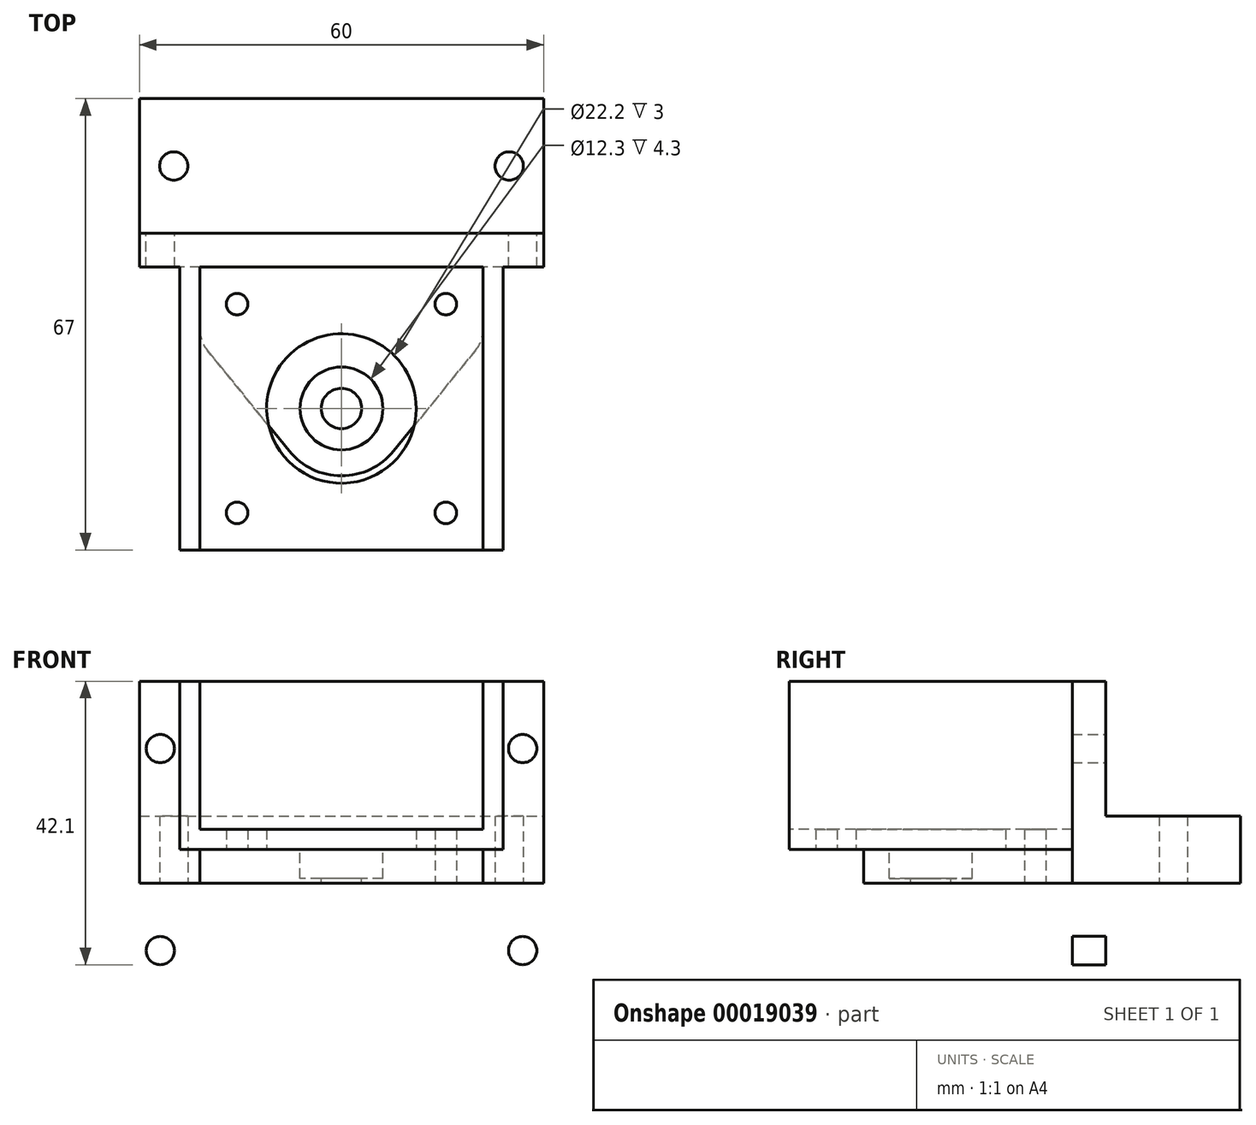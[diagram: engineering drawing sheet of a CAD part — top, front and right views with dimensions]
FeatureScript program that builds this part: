
annotation { "Feature Type Name" : "Feature", "Feature Type Description" : "" }
export const myFeature = defineFeature(function(context is Context, id is Id, definition is map)
    precondition{}
    {
        {
            var Q0;
            Q0=qCreatedBy(makeId("Top.planeOp"),FACE);
            var sketch = newSketch(context, id + "F0", { "sketchPlane" : qUnion([Q0])});
            skLineSegment(sketch, "E0.bottom", {"start": v(-30, 0) * mm, "end": v(30, 0) * mm});
            skLineSegment(sketch, "E0.top", {"start": v(-30, -20) * mm, "end": v(30, -20) * mm});
            skLineSegment(sketch, "E0.left", {"start": v(-30, 0) * mm, "end": v(-30, -20) * mm});
            skLineSegment(sketch, "E0.right", {"start": v(30, 0) * mm, "end": v(30, -20) * mm});
            skCircle(sketch, "E1", {"center": v(-24.9, -10) * mm, "radius": 2.1 * mm});
            skPoint(sketch, "E1.centerSnap0", {"position": v(-30, -10) * mm});
            skCircle(sketch, "E2.MirrorC", {"center": v(24.9, -10) * mm, "radius": 2.1 * mm});
            skLineSegment(sketch, "E3", {"start": v(-30, -20) * mm, "end": v(-30, -25) * mm});
            skLineSegment(sketch, "E4", {"start": v(-30, -25) * mm, "end": v(30, -25) * mm});
            skLineSegment(sketch, "E5", {"start": v(30, -25) * mm, "end": v(30, -20) * mm});
            skLineSegment(sketch, "E6.bottom", {"start": v(-21, -67) * mm, "end": v(21, -67) * mm});
            skCircle(sketch, "E7", {"center": v(-15.5, -30.5) * mm, "radius": 1.6 * mm});
            skCircle(sketch, "E8.MirrorC", {"center": v(15.5, -30.5) * mm, "radius": 1.6 * mm});
            skCircle(sketch, "E9", {"center": v(-15.5, -61.5) * mm, "radius": 1.6 * mm});
            skCircle(sketch, "E10.MirrorC", {"center": v(15.5, -61.5) * mm, "radius": 1.6 * mm});
            skLineSegment(sketch, "E11", {"start": v(15.5, -28.9) * mm, "end": v(15.5, -25) * mm, "construction": true});
            skLineSegment(sketch, "E12", {"start": v(15.5, -63.1) * mm, "end": v(15.5, -67) * mm, "construction": true});
            skLineSegment(sketch, "E13", {"start": v(-17.1, -30.5) * mm, "end": v(-21, -30.5) * mm, "construction": true});
            skLineSegment(sketch, "E14", {"start": v(-21, -25) * mm, "end": v(-21, -67) * mm});
            skLineSegment(sketch, "E15.MirrorCS", {"start": v(21, -25) * mm, "end": v(21, -67) * mm});
            skLineSegment(sketch, "E16", {"start": v(17.1, -30.5) * mm, "end": v(21, -30.5) * mm, "construction": true});
            skLineSegment(sketch, "E17", {"start": v(17.1, -61.5) * mm, "end": v(21, -61.5) * mm, "construction": true});
            skLineSegment(sketch, "E18.0", {"start": v(-24, -25) * mm, "end": v(-24, -67) * mm});
            skLineSegment(sketch, "E19.MirrorCS", {"start": v(24, -25) * mm, "end": v(24, -67) * mm});
            skLineSegment(sketch, "E20.0", {"start": v(-21, -70) * mm, "end": v(21, -70) * mm});
            skLineSegment(sketch, "E21", {"start": v(-24, -67) * mm, "end": v(-21, -70) * mm});
            skLineSegment(sketch, "E22", {"start": v(24, -67) * mm, "end": v(21, -70) * mm});
            skLineSegment(sketch, "E23", {"start": v(0, -67) * mm, "end": v(0, -25) * mm, "construction": true});
            skLineSegment(sketch, "E24", {"start": v(-21, -46) * mm, "end": v(21, -46) * mm, "construction": true});
            skCircle(sketch, "E25", {"center": v(0, -46) * mm, "radius": 11.1 * mm});
            skSolve(sketch);
        }
        {
            var Q0;
            Q0=makeQuery(id+"F0.imprint","IMPRINT",FACE,{"disambiguationData":[TD([[makeQuery(id+"F0.imprint","IMPRINT",EDGE,{"derivedFrom":sQuery(id+"F0.wireOp",EDGE,"E0.bottom")}),-1.0]])]});
            extrude(context, id + "F1", {"entities" : qUnion([Q0]), "depth" : 5 * mm});
        }
        {
            var Q0;
            Q0=makeQuery(id+"F1.opExtrude","SWEPT_FACE",FACE,{"disambiguationData":[OSD([sQuery(id+"F0.wireOp",EDGE,"E0.top")])]});
            var sketch = newSketch(context, id + "F2", { "sketchPlane" : qUnion([Q0])});
            skLineSegment(sketch, "E26.bottom", {"start": v(-30, 25) * mm, "end": v(30, 25) * mm});
            skLineSegment(sketch, "E26.top", {"start": v(-30, 5) * mm, "end": v(30, 5) * mm});
            skLineSegment(sketch, "E26.left", {"start": v(-30, 25) * mm, "end": v(-30, 5) * mm});
            skLineSegment(sketch, "E26.right", {"start": v(30, 25) * mm, "end": v(30, 5) * mm});
            skCircle(sketch, "E27", {"center": v(-26.9, 15) * mm, "radius": 2.1 * mm});
            skPoint(sketch, "E27.centerSnap0", {"position": v(-30, 15) * mm});
            skCircle(sketch, "E28.MirrorC", {"center": v(26.9, 15) * mm, "radius": 2.1 * mm});
            skLineSegment(sketch, "E29.0", {"start": v(-30, 5) * mm, "end": v(-30, 0) * mm});
            skLineSegment(sketch, "E29.1", {"start": v(-30, 0) * mm, "end": v(30, 0) * mm});
            skLineSegment(sketch, "E29.2", {"start": v(30, 5) * mm, "end": v(30, 0) * mm});
            skSolve(sketch);
        }
        {
            var Q0;
            Q0=makeQuery(id+"F2.imprint","IMPRINT",FACE,{"disambiguationData":[TD([[makeQuery(id+"F2.imprint","IMPRINT",EDGE,{"derivedFrom":sQuery(id+"F2.wireOp",EDGE,"E26.top")}),-1.0]])]});
            var Q1;
            Q1=makeQuery(id+"F2.imprint","IMPRINT",FACE,{"disambiguationData":[TD([[makeQuery(id+"F2.imprint","IMPRINT",EDGE,{"derivedFrom":sQuery(id+"F2.wireOp",EDGE,"E26.bottom")}),-1.0]])]});
            extrude(context, id + "F3", {"entities" : qUnion([Q0, Q1]), "operationType" : NewBodyOperationType.ADD, "depth" : 5 * mm});
        }
        {
            var Q0;
            Q0=makeQuery(id+"F0.imprint","IMPRINT",FACE,{"disambiguationData":[TD([[makeQuery(id+"F0.imprint","IMPRINT",EDGE,{"derivedFrom":sQuery(id+"F0.wireOp",EDGE,"E6.bottom")}),-1.0]])]});
            var Q1;
            Q1=makeQuery(id+"F3.opExtrude","SWEPT_FACE",FACE,{"disambiguationData":[OSD([sQuery(id+"F2.wireOp",EDGE,"E26.bottom")])]});
            extrude(context, id + "F4", {"entities" : qUnion([Q0]), "operationType" : NewBodyOperationType.ADD, "endBound" : BoundingType.UP_TO_SURFACE, "endBoundEntityFace" : qUnion([Q1]), "depth" : 25 * mm});
        }
        {
            var Q0;
            Q0=makeQuery(id+"F0.imprint","IMPRINT",FACE,{"disambiguationData":[TD([[makeQuery(id+"F0.imprint","IMPRINT",EDGE,{"derivedFrom":sQuery(id+"F0.wireOp",EDGE,"E6.bottom")}),1.0]])]});
            extrude(context, id + "F5", {"entities" : qUnion([Q0]), "operationType" : NewBodyOperationType.ADD, "depth" : 3 * mm});
        }
        {
            var Q0;
            Q0=makeQuery(id+"F4.opExtrude","SWEPT_FACE",FACE,{"disambiguationData":[OSD([sQuery(id+"F0.wireOp",EDGE,"E18.0")])]});
            var sketch = newSketch(context, id + "F6", { "sketchPlane" : qUnion([Q0])});
            skLineSegment(sketch, "E30.0", {"start": v(70, 25) * mm, "end": v(70, 0) * mm});
            skLineSegment(sketch, "E31", {"start": v(25, 0) * mm, "end": v(70, 0) * mm});
            skLineSegment(sketch, "E32", {"start": v(70, 0) * mm, "end": v(70, 6.9) * mm});
            skArc(sketch, "E33", {"start": v(25, 25) * mm, "mid": v(45.75, 11.6) * mm, "end": v(70, 6.9) * mm});
            skLineSegment(sketch, "E34.0", {"start": v(25, 25) * mm, "end": v(25, 0) * mm});
            skLineSegment(sketch, "E35.0", {"start": v(67, 25) * mm, "end": v(67, 0) * mm});
            skLineSegment(sketch, "E35.1", {"start": v(67, 25) * mm, "end": v(70, 25) * mm});
            skSolve(sketch);
        }
        {
            var Q0;
            {var subQ1=makeQuery(id+"F4.opExtrude","TWEAK_EDGE",EDGE,{"derivedFrom":[makeQuery(id+"F0.imprint","IMPRINT",EDGE,{"derivedFrom":sQuery(id+"F0.wireOp",EDGE,"E18.0")}),makeQuery(id+"F3.opExtrude","SWEPT_FACE",FACE,{"disambiguationData":[OSD([sQuery(id+"F2.wireOp",EDGE,"E26.bottom")])]})]});Q0=makeQuery(id+"F6.imprint","IMPRINT",FACE,{"disambiguationData":[TD([[makeQuery(id+"F6.imprint","IMPRINT",EDGE,{"derivedFrom":subQ1}),-1.0]])]});}
            var Q1;
            {var subQ4=sQuery(id+"F6.wireOp",EDGE,"E30.0");Q1=makeQuery(id+"F6.imprint","IMPRINT",FACE,{"disambiguationData":[TD([[makeQuery(id+"F6.imprint","IMPRINT",EDGE,{"derivedFrom":subQ4}),-1.0]])]});}
            extrude(context, id + "F7", {"entities" : qUnion([Q0, Q1]), "operationType" : NewBodyOperationType.REMOVE, "endBound" : BoundingType.THROUGH_ALL, "oppositeDirection" : true, "depth" : 25 * mm});
        }
        {
            var Q0;
            Q0=makeQuery(id+"F0.imprint","IMPRINT",FACE,{"disambiguationData":[TD([[makeQuery(id+"F0.imprint","IMPRINT",EDGE,{"derivedFrom":sQuery(id+"F0.wireOp",EDGE,"E0.bottom")}),-1.0]])]});
            extrude(context, id + "F8", {"entities" : qUnion([Q0]), "oppositeDirection" : true, "depth" : 5 * mm});
        }
        {
            var Q0;
            Q0=makeQuery(id+"F0.imprint","IMPRINT",FACE,{"disambiguationData":[TD([[makeQuery(id+"F0.imprint","IMPRINT",EDGE,{"derivedFrom":sQuery(id+"F0.wireOp",EDGE,"E6.bottom")}),1.0]])]});
            var sketch = newSketch(context, id + "F9", { "sketchPlane" : qUnion([Q0])});
            skPoint(sketch, "E36.0", {"position": v(0, -46) * mm});
            skCircle(sketch, "E37", {"center": v(0, -46) * mm, "radius": 6.15 * mm});
            skLineSegment(sketch, "E38", {"start": v(30, -25) * mm, "end": v(7.75, -52.31) * mm});
            skLineSegment(sketch, "E39", {"start": v(-30, -25) * mm, "end": v(-7.75, -52.31) * mm});
            skArc(sketch, "E40", {"start": v(-7.75, -52.31) * mm, "mid": v(0, -56) * mm, "end": v(7.75, -52.31) * mm});
            skLineSegment(sketch, "E41.0", {"start": v(30, 0) * mm, "end": v(30, -25) * mm});
            skLineSegment(sketch, "E41.1", {"start": v(-30, 0) * mm, "end": v(-30, -25) * mm});
            skLineSegment(sketch, "E42.0", {"start": v(-30, -20) * mm, "end": v(30, -20) * mm});
            skLineSegment(sketch, "E43", {"start": v(30, -25) * mm, "end": v(-30, -25) * mm});
            skCircle(sketch, "E44", {"center": v(0, -46) * mm, "radius": 3 * mm});
            skSolve(sketch);
        }
        {
            var Q0;
            {var subQ7=sQuery(id+"F9.wireOp",EDGE,"E42.0");Q0=makeQuery(id+"F9.imprint","IMPRINT",FACE,{"disambiguationData":[TD([[makeQuery(id+"F9.imprint","IMPRINT",EDGE,{"derivedFrom":subQ7}),-1.0]])]});}
            extrude(context, id + "F10", {"entities" : qUnion([Q0]), "operationType" : NewBodyOperationType.ADD, "oppositeDirection" : true, "depth" : 25 * mm});
        }
        {
            var Q0;
            Q0=makeQuery(id+"F9.imprint","IMPRINT",FACE,{"disambiguationData":[TD([[makeQuery(id+"F9.imprint","IMPRINT",EDGE,{"derivedFrom":makeQuery(id+"F0.imprint","IMPRINT",EDGE,{"derivedFrom":sQuery(id+"F0.wireOp",EDGE,"E7")})}),-1.0]])]});
            var Q1;
            {var subQ10=sQuery(id+"F9.wireOp",EDGE,"f1a987d3-3d6a-4107-b72d-43f94a35c171.0");Q1=makeQuery(id+"F9.imprint","IMPRINT",FACE,{"disambiguationData":[TD([[makeQuery(id+"F9.imprint","IMPRINT",EDGE,{"derivedFrom":subQ10}),-1.0]])]});}
            var Q2;
            Q2=makeQuery(id+"F9.imprint","IMPRINT",FACE,{"disambiguationData":[TD([[makeQuery(id+"F9.imprint","IMPRINT",EDGE,{"derivedFrom":sQuery(id+"F9.wireOp",EDGE,"E37")}),1.0]])]});
            var Q3;
            Q3=makeQuery(id+"F9.imprint","IMPRINT",FACE,{"disambiguationData":[TD([[makeQuery(id+"F9.imprint","IMPRINT",EDGE,{"derivedFrom":sQuery(id+"F9.wireOp",EDGE,"E37")}),-1.0]])]});
            var Q4;
            Q4=makeQuery(id+"F9.imprint","IMPRINT",FACE,{"disambiguationData":[TD([[makeQuery(id+"F9.imprint","IMPRINT",EDGE,{"derivedFrom":makeQuery(id+"F0.imprint","IMPRINT",EDGE,{"derivedFrom":sQuery(id+"F0.wireOp",EDGE,"E7")})}),1.0]])]});
            var Q5;
            Q5=makeQuery(id+"F9.imprint","IMPRINT",FACE,{"disambiguationData":[TD([[makeQuery(id+"F9.imprint","IMPRINT",EDGE,{"derivedFrom":makeQuery(id+"F0.imprint","IMPRINT",EDGE,{"derivedFrom":sQuery(id+"F0.wireOp",EDGE,"E8.MirrorC")})}),-1.0]])]});
            var Q6;
            Q6=makeQuery(id+"F10.opExtrude","CAP_FACE",FACE,{"disambiguationData":[OSD([sQuery(id+"F9.wireOp",EDGE,"E41.0"),sQuery(id+"F9.wireOp",EDGE,"E41.1"),sQuery(id+"F9.wireOp",EDGE,"E42.0"),sQuery(id+"F9.wireOp",EDGE,"E43")])],"isStart":false});
            extrude(context, id + "F11", {"entities" : qUnion([Q0, Q1, Q2, Q3, Q4, Q5]), "operationType" : NewBodyOperationType.ADD, "endBound" : BoundingType.UP_TO_SURFACE, "oppositeDirection" : true, "endBoundEntityFace" : qUnion([Q6]), "depth" : 5.5 * mm});
        }
        {
            var Q0;
            Q0=makeQuery(id+"F9.imprint","IMPRINT",FACE,{"disambiguationData":[TD([[makeQuery(id+"F9.imprint","IMPRINT",EDGE,{"derivedFrom":sQuery(id+"F9.wireOp",EDGE,"E44")}),1.0]])]});
            var Q1;
            Q1=sQuery(id+"F9.wireOp",EDGE,"E37");
            extrude(context, id + "F12", {"entities" : qUnion([Q0]), "operationType" : NewBodyOperationType.REMOVE, "surfaceEntities" : qUnion([Q1]), "endBound" : BoundingType.THROUGH_ALL, "oppositeDirection" : true, "depth" : 4 * mm});
        }
        {
            var Q0;
            Q0=makeQuery(id+"F10.opExtrude","SWEPT_FACE",FACE,{"disambiguationData":[OSD([sQuery(id+"F9.wireOp",EDGE,"E42.0")])]});
            var sketch = newSketch(context, id + "F13", { "sketchPlane" : qUnion([Q0])});
            skCircle(sketch, "E45.0", {"center": v(26.9, 15) * mm, "radius": 2.1 * mm, "construction": true});
            skCircle(sketch, "E45.1", {"center": v(-26.9, 15) * mm, "radius": 2.1 * mm, "construction": true});
            skCircle(sketch, "E46.MirrorC", {"center": v(26.9, -15) * mm, "radius": 2.1 * mm});
            skCircle(sketch, "E47.MirrorC", {"center": v(-26.9, -15) * mm, "radius": 2.1 * mm});
            skSolve(sketch);
        }
        {
            var Q0;
            Q0=makeQuery(id+"F13.imprint","IMPRINT",FACE,{"disambiguationData":[TD([[makeQuery(id+"F13.imprint","IMPRINT",EDGE,{"derivedFrom":sQuery(id+"F13.wireOp",EDGE,"E46.MirrorC")}),-1.0]])]});
            var Q1;
            Q1=makeQuery(id+"F13.imprint","IMPRINT",FACE,{"disambiguationData":[TD([[makeQuery(id+"F13.imprint","IMPRINT",EDGE,{"derivedFrom":sQuery(id+"F13.wireOp",EDGE,"E47.MirrorC")}),-1.0]])]});
            extrude(context, id + "F14", {"entities" : qUnion([Q0, Q1]), "operationType" : NewBodyOperationType.REMOVE, "endBound" : BoundingType.THROUGH_ALL, "oppositeDirection" : true, "depth" : 25 * mm});
        }
        {
            var Q0;
            Q0=makeQuery(id+"F11.opExtrude","SWEPT_FACE",FACE,{"disambiguationData":[OSD([sQuery(id+"F0.wireOp",EDGE,"E14")])]});
            var sketch = newSketch(context, id + "F15", { "sketchPlane" : qUnion([Q0])});
            skLineSegment(sketch, "E48.0", {"start": v(25, -25) * mm, "end": v(25, 0) * mm});
            skLineSegment(sketch, "E48.1", {"start": v(52.31, 0) * mm, "end": v(56, 0) * mm});
            skLineSegment(sketch, "E48.2", {"start": v(25, 0) * mm, "end": v(52.31, 0) * mm});
            skLineSegment(sketch, "E49", {"start": v(56, 0) * mm, "end": v(56, -5.5) * mm});
            skArc(sketch, "E50", {"start": v(56, -5.5) * mm, "mid": v(38.65, -12.3) * mm, "end": v(25, -25) * mm});
            skLineSegment(sketch, "E51", {"start": v(56, -5.5) * mm, "end": v(56, -25) * mm});
            skPoint(sketch, "E51.endSnap0", {"position": v(30.53, -25) * mm});
            skLineSegment(sketch, "E52", {"start": v(56, -25) * mm, "end": v(25, -25) * mm});
            skSolve(sketch);
        }
        {
            var Q0;
            {var subQ5=sQuery(id+"F15.wireOp",EDGE,"E51");Q0=makeQuery(id+"F15.imprint","IMPRINT",FACE,{"disambiguationData":[TD([[makeQuery(id+"F15.imprint","IMPRINT",EDGE,{"derivedFrom":subQ5}),-1.0]])]});}
            var Q1;
            {var subQ1=sQuery(id+"F15.wireOp",EDGE,"E50");var subQ3=sQuery(id+"F15.wireOp",EDGE,"E52");var subQ5=makeQuery(id+"F15.imprint","INTERSECT",VERTEX,{"derivedFrom":[sQuery(id+"F15.wireOp",EDGE,"E48.0"),subQ1,subQ3]});Q1=makeQuery(id+"F15.imprint","IMPRINT",FACE,{"disambiguationData":[TD([[makeQuery(id+"F15.imprint","IMPRINT",EDGE,{"disambiguationData":[TD([[subQ5,1.0]])],"derivedFrom":subQ1}),1.0]])]});}
            extrude(context, id + "F16", {"entities" : qUnion([Q0, Q1]), "operationType" : NewBodyOperationType.REMOVE, "endBound" : BoundingType.THROUGH_ALL, "oppositeDirection" : true, "depth" : 25 * mm});
        }
        {
            var Q0;
            Q0=makeQuery(id+"F11.opExtrude","SWEPT_EDGE",EDGE,{"disambiguationData":[OSD([sQuery(id+"F0.wireOp",EDGE,"E15.MirrorCS"),sQuery(id+"F9.wireOp",EDGE,"E38")])]});
            var Q1;
            Q1=makeQuery(id+"F11.opExtrude","SWEPT_EDGE",EDGE,{"disambiguationData":[OSD([sQuery(id+"F0.wireOp",EDGE,"E14"),sQuery(id+"F9.wireOp",EDGE,"E39")])]});
            var Q2;
            Q2=makeQuery(id+"F16.boolean.opBoolean","INTERSECT",EDGE,{"derivedFrom":[makeQuery(id+"F11.opExtrude","SWEPT_FACE",FACE,{"disambiguationData":[OSD([sQuery(id+"F9.wireOp",EDGE,"E38")])]}),makeQuery(id+"F16.opExtrude","SWEPT_FACE",FACE,{"disambiguationData":[OSD([sQuery(id+"F15.wireOp",EDGE,"E50")])]})]});
            fillet(context, id + "F17", {"entities" : qUnion([Q0, Q1, Q2]), "radius" : 5 * mm, "tangentPropagation" : true, "allowEdgeOverflow" : false});
        }
        {
            var Q0;
            Q0=makeQuery(id+"F9.imprint","IMPRINT",FACE,{"disambiguationData":[TD([[makeQuery(id+"F9.imprint","IMPRINT",EDGE,{"derivedFrom":sQuery(id+"F9.wireOp",EDGE,"E37")}),1.0]])]});
            extrude(context, id + "F18", {"entities" : qUnion([Q0]), "operationType" : NewBodyOperationType.REMOVE, "oppositeDirection" : true, "depth" : 4.3 * mm});
        }
    });
